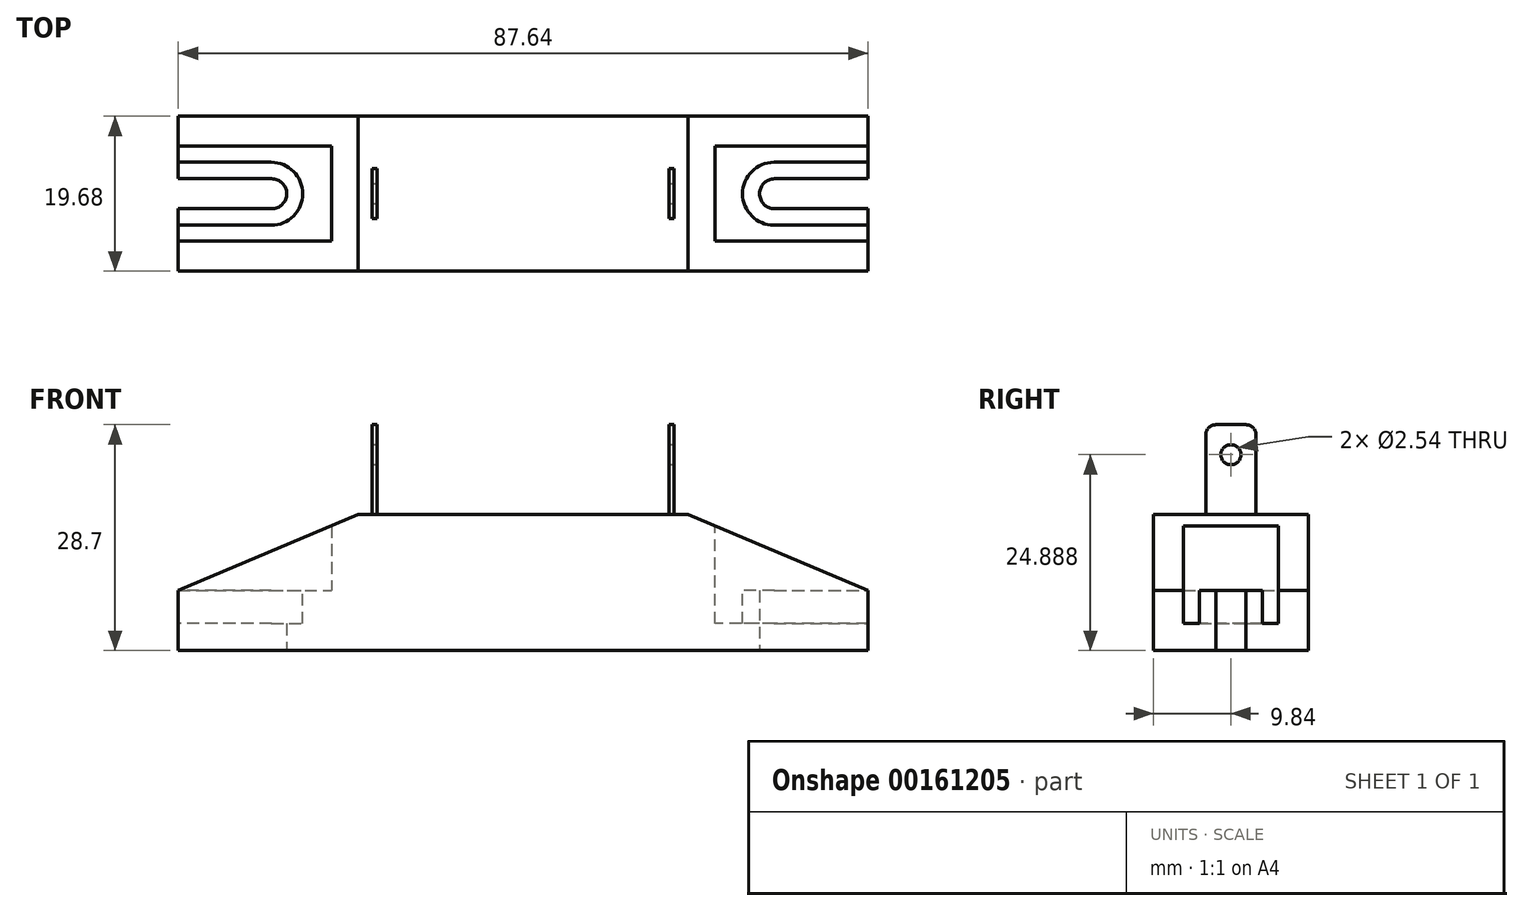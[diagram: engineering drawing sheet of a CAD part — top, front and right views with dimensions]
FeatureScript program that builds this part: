
annotation { "Feature Type Name" : "Feature", "Feature Type Description" : "" }
export const myFeature = defineFeature(function(context is Context, id is Id, definition is map)
    precondition{}
    {
        {
            var Q0;
            Q0=qCreatedBy(makeId("Front.planeOp"),FACE);
            var sketch = newSketch(context, id + "F0", { "sketchPlane" : qUnion([Q0])});
            skLineSegment(sketch, "E0", {"start": v(-43.82, 0) * mm, "end": v(43.82, 0) * mm});
            skLineSegment(sketch, "E1", {"start": v(-43.82, 0) * mm, "end": v(-43.82, 7.62) * mm});
            skLineSegment(sketch, "E2", {"start": v(-43.82, 7.62) * mm, "end": v(-20.96, 17.27) * mm});
            skLineSegment(sketch, "E3", {"start": v(-20.96, 17.27) * mm, "end": v(20.96, 17.27) * mm});
            skLineSegment(sketch, "E4", {"start": v(20.96, 17.27) * mm, "end": v(43.82, 7.62) * mm});
            skLineSegment(sketch, "E5", {"start": v(43.82, 7.62) * mm, "end": v(43.82, 0) * mm});
            skLineSegment(sketch, "E6", {"start": v(0, 26.65) * mm, "end": v(0, -8.99) * mm, "construction": true});
            skPoint(sketch, "E7", {"position": v(0, 17.27) * mm});
            skSolve(sketch);
        }
        {
            var Q0;
            Q0=makeQuery(id+"F0.imprint","IMPRINT",FACE,{"disambiguationData":[TD([[makeQuery(id+"F0.imprint","IMPRINT",EDGE,{"derivedFrom":sQuery(id+"F0.wireOp",EDGE,"E0")}),1.0]])]});
            extrude(context, id + "F1", {"entities" : qUnion([Q0]), "endBound" : BoundingType.SYMMETRIC, "depth" : 19.68 * mm});
        }
        {
            var Q0;
            Q0=qCreatedBy(makeId("Top.planeOp"),FACE);
            var sketch = newSketch(context, id + "F2", { "sketchPlane" : qUnion([Q0])});
            skLineSegment(sketch, "E8", {"start": v(-54.85, 0) * mm, "end": v(57.23, 0) * mm, "construction": true});
            skArc(sketch, "E9", {"start": v(-31.94, -1.9) * mm, "mid": v(-30.04, 0) * mm, "end": v(-31.94, 1.9) * mm});
            skLineSegment(sketch, "E10", {"start": v(-31.94, 1.9) * mm, "end": v(-44.44, 1.9) * mm});
            skLineSegment(sketch, "E11", {"start": v(-31.94, -1.9) * mm, "end": v(-44.44, -1.9) * mm});
            skLineSegment(sketch, "E12", {"start": v(-44.44, 1.9) * mm, "end": v(-44.44, -1.9) * mm});
            skArc(sketch, "E13", {"start": v(-31.94, -4) * mm, "mid": v(-27.94, 0) * mm, "end": v(-31.94, 4) * mm});
            skLineSegment(sketch, "E14", {"start": v(-31.94, 4) * mm, "end": v(-45.54, 4) * mm});
            skLineSegment(sketch, "E15", {"start": v(-31.94, -4) * mm, "end": v(-45.44, -4) * mm});
            skLineSegment(sketch, "E16", {"start": v(-45.44, -4) * mm, "end": v(-45.44, 4) * mm});
            skLineSegment(sketch, "E17.MirrorCS", {"start": v(31.94, 4) * mm, "end": v(45.54, 4) * mm});
            skArc(sketch, "E18.MirrorCS", {"start": v(31.94, -4) * mm, "mid": v(27.94, 0) * mm, "end": v(31.94, 4) * mm});
            skLineSegment(sketch, "E19.MirrorCS", {"start": v(31.94, -4) * mm, "end": v(45.44, -4) * mm});
            skLineSegment(sketch, "E20.MirrorCS", {"start": v(45.44, -4) * mm, "end": v(45.44, 4) * mm});
            skLineSegment(sketch, "E21.MirrorCS", {"start": v(31.94, 1.9) * mm, "end": v(44.44, 1.9) * mm});
            skArc(sketch, "E22.MirrorCS", {"start": v(31.94, -1.9) * mm, "mid": v(30.04, 0) * mm, "end": v(31.94, 1.9) * mm});
            skLineSegment(sketch, "E23.MirrorCS", {"start": v(31.94, -1.9) * mm, "end": v(44.44, -1.9) * mm});
            skLineSegment(sketch, "E24.MirrorCS", {"start": v(44.44, 1.9) * mm, "end": v(44.44, -1.9) * mm});
            skSolve(sketch);
        }
        {
            var Q0;
            Q0=makeQuery(id+"F2.imprint","IMPRINT",FACE,{"disambiguationData":[TD([[makeQuery(id+"F2.imprint","IMPRINT",EDGE,{"derivedFrom":sQuery(id+"F2.wireOp",EDGE,"E9")}),1.0]])]});
            var Q1;
            Q1=makeQuery(id+"F2.imprint","IMPRINT",FACE,{"disambiguationData":[TD([[makeQuery(id+"F2.imprint","IMPRINT",EDGE,{"derivedFrom":sQuery(id+"F2.wireOp",EDGE,"E21.MirrorCS")}),-1.0]])]});
            extrude(context, id + "F3", {"entities" : qUnion([Q0, Q1]), "operationType" : NewBodyOperationType.REMOVE, "depth" : 25.4 * mm});
        }
        {
            var Q0;
            Q0=qCreatedBy(makeId("Top.planeOp"),FACE);
            cPlane(context, id + "F4", {"entities" : qUnion([Q0]), "cplaneType" : CPlaneType.OFFSET, "offset" : 7.62 * mm, "width" : 152.4 * mm, "height" : 152.4 * mm});
        }
        {
            var Q0;
            Q0=qCreatedBy(id+"F4.planeOp",FACE);
            var sketch = newSketch(context, id + "F5", { "sketchPlane" : qUnion([Q0])});
            skLineSegment(sketch, "E25", {"start": v(-54.92, 0) * mm, "end": v(57.16, 0) * mm, "construction": true});
            skArc(sketch, "E26", {"start": v(-32.01, -1.9) * mm, "mid": v(-30.1, 0) * mm, "end": v(-32.01, 1.9) * mm});
            skLineSegment(sketch, "E27", {"start": v(-32.01, 1.9) * mm, "end": v(-44.5, 1.9) * mm});
            skLineSegment(sketch, "E28", {"start": v(-32.01, -1.9) * mm, "end": v(-44.5, -1.9) * mm});
            skLineSegment(sketch, "E29", {"start": v(-44.5, 1.9) * mm, "end": v(-44.5, -1.9) * mm});
            skArc(sketch, "E30", {"start": v(-32.01, -4) * mm, "mid": v(-28.01, 0) * mm, "end": v(-32.01, 4) * mm});
            skLineSegment(sketch, "E31", {"start": v(-32.01, 4) * mm, "end": v(-45.6, 4) * mm});
            skLineSegment(sketch, "E32", {"start": v(-32.01, -4) * mm, "end": v(-45.51, -4) * mm});
            skLineSegment(sketch, "E33", {"start": v(-45.51, -4) * mm, "end": v(-45.51, 4) * mm});
            skLineSegment(sketch, "E34.MirrorCS", {"start": v(31.87, 4) * mm, "end": v(45.47, 4) * mm});
            skArc(sketch, "E35.MirrorCS", {"start": v(31.87, -4) * mm, "mid": v(27.87, 0) * mm, "end": v(31.87, 4) * mm});
            skLineSegment(sketch, "E36.MirrorCS", {"start": v(31.87, -4) * mm, "end": v(45.37, -4) * mm});
            skLineSegment(sketch, "E37.MirrorCS", {"start": v(45.37, -4) * mm, "end": v(45.37, 4) * mm});
            skLineSegment(sketch, "E38.MirrorCS", {"start": v(31.87, 1.9) * mm, "end": v(44.37, 1.9) * mm});
            skArc(sketch, "E39.MirrorCS", {"start": v(31.87, -1.9) * mm, "mid": v(29.97, 0) * mm, "end": v(31.87, 1.9) * mm});
            skLineSegment(sketch, "E40.MirrorCS", {"start": v(31.87, -1.9) * mm, "end": v(44.37, -1.9) * mm});
            skLineSegment(sketch, "E41.MirrorCS", {"start": v(44.37, 1.9) * mm, "end": v(44.37, -1.9) * mm});
            skLineSegment(sketch, "E42", {"start": v(-46.74, 6.03) * mm, "end": v(-24.35, 6.03) * mm});
            skLineSegment(sketch, "E43", {"start": v(-24.35, 6.03) * mm, "end": v(-24.35, -6.03) * mm});
            skLineSegment(sketch, "E44", {"start": v(-24.35, -6.03) * mm, "end": v(-46.74, -6.03) * mm});
            skLineSegment(sketch, "E45", {"start": v(-46.74, -6.03) * mm, "end": v(-46.74, 6.03) * mm});
            skPoint(sketch, "E46", {"position": v(-24.35, 0) * mm});
            skLineSegment(sketch, "E47.MirrorCS", {"start": v(46.74, 6.03) * mm, "end": v(24.35, 6.03) * mm});
            skLineSegment(sketch, "E48.MirrorCS", {"start": v(24.35, 6.03) * mm, "end": v(24.35, -6.03) * mm});
            skLineSegment(sketch, "E49.MirrorCS", {"start": v(24.35, -6.03) * mm, "end": v(46.74, -6.03) * mm});
            skLineSegment(sketch, "E50.MirrorCS", {"start": v(46.74, -6.03) * mm, "end": v(46.74, 6.03) * mm});
            skSolve(sketch);
        }
        {
            var Q0;
            Q0=makeQuery(id+"F5.imprint","IMPRINT",FACE,{"disambiguationData":[TD([[makeQuery(id+"F5.imprint","IMPRINT",EDGE,{"derivedFrom":sQuery(id+"F5.wireOp",EDGE,"E26")}),-1.0]])]});
            var Q1;
            {var subQ1=sQuery(id+"F5.wireOp",EDGE,"E35.MirrorCS");Q1=makeQuery(id+"F5.imprint","IMPRINT",FACE,{"disambiguationData":[TD([[makeQuery(id+"F5.imprint","IMPRINT",EDGE,{"derivedFrom":subQ1}),-1.0]])]});}
            extrude(context, id + "F6", {"entities" : qUnion([Q0, Q1]), "operationType" : NewBodyOperationType.REMOVE, "oppositeDirection" : true, "depth" : 4.2 * mm});
        }
        {
            var Q0;
            {var subQ2=sQuery(id+"F5.wireOp",EDGE,"E30");Q0=makeQuery(id+"F5.imprint","IMPRINT",FACE,{"disambiguationData":[TD([[makeQuery(id+"F5.imprint","IMPRINT",EDGE,{"derivedFrom":subQ2}),-1.0]])]});}
            var Q1;
            Q1=makeQuery(id+"F5.imprint","IMPRINT",FACE,{"disambiguationData":[TD([[makeQuery(id+"F5.imprint","IMPRINT",EDGE,{"derivedFrom":sQuery(id+"F5.wireOp",EDGE,"E26")}),-1.0]])]});
            var Q2;
            Q2=makeQuery(id+"F5.imprint","IMPRINT",FACE,{"disambiguationData":[TD([[makeQuery(id+"F5.imprint","IMPRINT",EDGE,{"derivedFrom":sQuery(id+"F5.wireOp",EDGE,"E26")}),1.0]])]});
            var Q3;
            {var subQ1=sQuery(id+"F5.wireOp",EDGE,"E35.MirrorCS");Q3=makeQuery(id+"F5.imprint","IMPRINT",FACE,{"disambiguationData":[TD([[makeQuery(id+"F5.imprint","IMPRINT",EDGE,{"derivedFrom":subQ1}),1.0]])]});}
            var Q4;
            {var subQ1=sQuery(id+"F5.wireOp",EDGE,"E35.MirrorCS");Q4=makeQuery(id+"F5.imprint","IMPRINT",FACE,{"disambiguationData":[TD([[makeQuery(id+"F5.imprint","IMPRINT",EDGE,{"derivedFrom":subQ1}),-1.0]])]});}
            var Q5;
            Q5=makeQuery(id+"F5.imprint","IMPRINT",FACE,{"disambiguationData":[TD([[makeQuery(id+"F5.imprint","IMPRINT",EDGE,{"derivedFrom":sQuery(id+"F5.wireOp",EDGE,"E38.MirrorCS")}),-1.0]])]});
            extrude(context, id + "F7", {"entities" : qUnion([Q0, Q1, Q2, Q3, Q4, Q5]), "operationType" : NewBodyOperationType.REMOVE, "depth" : 12.7 * mm});
        }
        {
            var Q0;
            Q0=makeQuery(id+"F1.opExtrude","SWEPT_FACE",FACE,{"disambiguationData":[OSD([sQuery(id+"F0.wireOp",EDGE,"E3")])]});
            var sketch = newSketch(context, id + "F8", { "sketchPlane" : qUnion([Q0])});
            skLineSegment(sketch, "E51.bottom", {"start": v(-18.54, 3.18) * mm, "end": v(-19.18, 3.18) * mm});
            skLineSegment(sketch, "E51.top", {"start": v(-18.54, -3.17) * mm, "end": v(-19.18, -3.17) * mm});
            skLineSegment(sketch, "E51.left", {"start": v(-18.54, 3.18) * mm, "end": v(-18.54, -3.17) * mm});
            skLineSegment(sketch, "E51.right", {"start": v(-19.18, 3.18) * mm, "end": v(-19.18, -3.17) * mm});
            skPoint(sketch, "E51.middle", {"position": v(-18.86, 0) * mm});
            skLineSegment(sketch, "E52.MirrorCS", {"start": v(19.18, 3.18) * mm, "end": v(19.18, -3.17) * mm});
            skLineSegment(sketch, "E53.MirrorCS", {"start": v(18.54, 3.18) * mm, "end": v(19.18, 3.18) * mm});
            skLineSegment(sketch, "E54.MirrorCS", {"start": v(18.54, 3.18) * mm, "end": v(18.54, -3.17) * mm});
            skLineSegment(sketch, "E55.MirrorCS", {"start": v(18.54, -3.17) * mm, "end": v(19.18, -3.17) * mm});
            skSolve(sketch);
        }
        {
            var Q0;
            Q0=makeQuery(id+"F8.imprint","IMPRINT",FACE,{"disambiguationData":[TD([[makeQuery(id+"F8.imprint","IMPRINT",EDGE,{"derivedFrom":sQuery(id+"F8.wireOp",EDGE,"E51.bottom")}),1.0]])]});
            var Q1;
            Q1=makeQuery(id+"F8.imprint","IMPRINT",FACE,{"disambiguationData":[TD([[makeQuery(id+"F8.imprint","IMPRINT",EDGE,{"derivedFrom":sQuery(id+"F8.wireOp",EDGE,"E52.MirrorCS")}),-1.0]])]});
            extrude(context, id + "F9", {"entities" : qUnion([Q0, Q1]), "operationType" : NewBodyOperationType.ADD, "depth" : 11.43 * mm});
        }
        {
            var Q0;
            Q0=makeQuery(id+"F9.opExtrude","SWEPT_FACE",FACE,{"disambiguationData":[OSD([sQuery(id+"F8.wireOp",EDGE,"E52.MirrorCS")])]});
            var sketch = newSketch(context, id + "F10", { "sketchPlane" : qUnion([Q0])});
            skCircle(sketch, "E56", {"center": v(0, 24.89) * mm, "radius": 1.27 * mm});
            skSolve(sketch);
        }
        {
            var Q0;
            Q0=makeQuery(id+"F10.imprint","IMPRINT",FACE,{"disambiguationData":[TD([[makeQuery(id+"F10.imprint","IMPRINT",EDGE,{"derivedFrom":sQuery(id+"F10.wireOp",EDGE,"E56")}),1.0]])]});
            extrude(context, id + "F11", {"entities" : qUnion([Q0]), "operationType" : NewBodyOperationType.REMOVE, "oppositeDirection" : true, "depth" : 40.64 * mm});
        }
        {
            var Q0;
            Q0=makeQuery(id+"F9.opExtrude","CAP_EDGE",EDGE,{"disambiguationData":[OSD([sQuery(id+"F8.wireOp",EDGE,"E55.MirrorCS")])],"isStart":false});
            var Q1;
            Q1=makeQuery(id+"F9.opExtrude","CAP_EDGE",EDGE,{"disambiguationData":[OSD([sQuery(id+"F8.wireOp",EDGE,"E53.MirrorCS")])],"isStart":false});
            var Q2;
            Q2=makeQuery(id+"F9.opExtrude","CAP_EDGE",EDGE,{"disambiguationData":[OSD([sQuery(id+"F8.wireOp",EDGE,"E51.bottom")])],"isStart":false});
            var Q3;
            Q3=makeQuery(id+"F9.opExtrude","CAP_EDGE",EDGE,{"disambiguationData":[OSD([sQuery(id+"F8.wireOp",EDGE,"E51.top")])],"isStart":false});
            fillet(context, id + "F12", {"entities" : qUnion([Q0, Q1, Q2, Q3]), "radius" : 1.27 * mm, "tangentPropagation" : true, "allowEdgeOverflow" : false});
        }
    });
